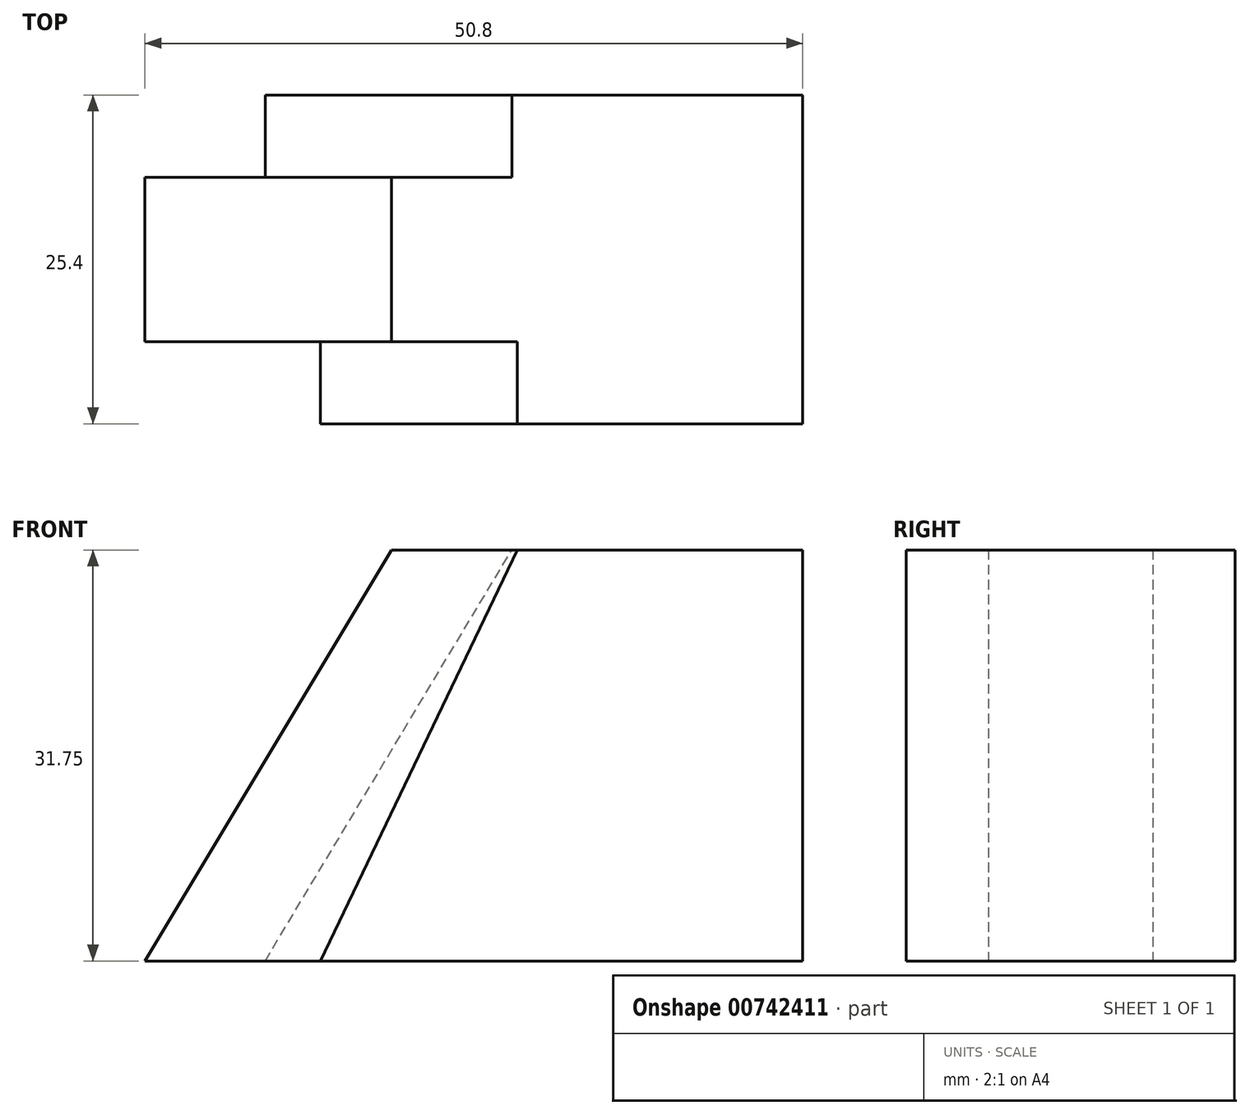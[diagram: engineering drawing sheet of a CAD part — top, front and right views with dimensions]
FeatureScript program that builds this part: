
annotation { "Feature Type Name" : "Feature", "Feature Type Description" : "" }
export const myFeature = defineFeature(function(context is Context, id is Id, definition is map)
    precondition{}
    {
        {
            var Q0;
            Q0=qCreatedBy(makeId("Front.planeOp"),FACE);
            var sketch = newSketch(context, id + "F0", { "sketchPlane" : qUnion([Q0])});
            skLineSegment(sketch, "E0", {"start": v(0, 31.75) * mm, "end": v(0, 0) * mm});
            skLineSegment(sketch, "E1", {"start": v(0, 0) * mm, "end": v(50.8, 0) * mm});
            skLineSegment(sketch, "E2", {"start": v(50.8, 0) * mm, "end": v(50.8, 31.75) * mm});
            skLineSegment(sketch, "E3", {"start": v(50.8, 31.75) * mm, "end": v(0, 31.75) * mm});
            skLineSegment(sketch, "E4", {"start": v(21.23, 31.75) * mm, "end": v(37.56, 0) * mm});
            skLineSegment(sketch, "E5", {"start": v(50.8, 0) * mm, "end": v(34.47, 31.75) * mm});
            skSolve(sketch);
        }
        {
            var Q0;
            Q0 = qSketchRegion(id + "F0", true);
            extrude(context, id + "F1", {"entities" : qUnion([Q0]), "oppositeDirection" : true, "depth" : 25.4 * mm, "offsetDistance" : 25.4 * mm});
        }
        {
            var Q0;
            Q0=qCreatedBy(makeId("Front.planeOp"),FACE);
            var sketch = newSketch(context, id + "F2", { "sketchPlane" : qUnion([Q0])});
            skLineSegment(sketch, "E6", {"start": v(28.91, 32.08) * mm, "end": v(13.54, 0) * mm});
            skLineSegment(sketch, "E7", {"start": v(28.91, 32.08) * mm, "end": v(0, 32.08) * mm});
            skLineSegment(sketch, "E8", {"start": v(0, 32.08) * mm, "end": v(0, 0) * mm});
            skLineSegment(sketch, "E9", {"start": v(0, 0) * mm, "end": v(13.54, 0) * mm});
            skSolve(sketch);
        }
        {
            var Q0;
            Q0 = qSketchRegion(id + "F2", true);
            extrude(context, id + "F3", {"entities" : qUnion([Q0]), "operationType" : NewBodyOperationType.REMOVE, "endBound" : BoundingType.SYMMETRIC, "oppositeDirection" : true, "depth" : 12.7 * mm, "offsetDistance" : 25.4 * mm});
        }
        {
            var Q0;
            Q0=makeQuery(id+"F1.opExtrude","CAP_FACE",FACE,{"disambiguationData":[OSD([sQuery(id+"F0.wireOp",EDGE,"E0"),sQuery(id+"F0.wireOp",EDGE,"E1"),sQuery(id+"F0.wireOp",EDGE,"E2"),sQuery(id+"F0.wireOp",EDGE,"E3")])],"isStart":false});
            var sketch = newSketch(context, id + "F4", { "sketchPlane" : qUnion([Q0])});
            skLineSegment(sketch, "E10", {"start": v(-19.05, 31.75) * mm, "end": v(0, 0) * mm});
            skSolve(sketch);
        }
        {
            var Q0;
            {var subQ0=sQuery(id+"F4.wireOp",EDGE,"E10");Q0=makeQuery(id+"F4.imprint","IMPRINT",FACE,{"disambiguationData":[TD([[makeQuery(id+"F4.imprint","IMPRINT",EDGE,{"derivedFrom":subQ0}),1.0]])]});}
            extrude(context, id + "F5", {"entities" : qUnion([Q0]), "operationType" : NewBodyOperationType.REMOVE, "endBound" : BoundingType.THROUGH_ALL, "oppositeDirection" : true, "depth" : 25.4 * mm, "offsetDistance" : 25.4 * mm});
        }
        {
            var Q0;
            Q0=makeQuery(id+"F1.opExtrude","CAP_FACE",FACE,{"disambiguationData":[OSD([sQuery(id+"F0.wireOp",EDGE,"E0"),sQuery(id+"F0.wireOp",EDGE,"E1"),sQuery(id+"F0.wireOp",EDGE,"E2"),sQuery(id+"F0.wireOp",EDGE,"E3")])],"isStart":false});
            var sketch = newSketch(context, id + "F6", { "sketchPlane" : qUnion([Q0])});
            skLineSegment(sketch, "E11", {"start": v(-28.33, 31.75) * mm, "end": v(-9.28, 0) * mm});
            skSolve(sketch);
        }
        {
            var Q0;
            Q0 = qSketchRegion(id + "F6", true);
            var Q1;
            {var subQ0=sQuery(id+"F6.wireOp",EDGE,"E11");Q1=makeQuery(id+"F6.imprint","IMPRINT",FACE,{"disambiguationData":[TD([[makeQuery(id+"F6.imprint","IMPRINT",EDGE,{"derivedFrom":subQ0}),1.0]])]});}
            extrude(context, id + "F7", {"entities" : qUnion([Q0, Q1]), "operationType" : NewBodyOperationType.REMOVE, "endBound" : BoundingType.SYMMETRIC, "oppositeDirection" : true, "depth" : 12.7 * mm, "offsetDistance" : 25.4 * mm});
        }
    });
